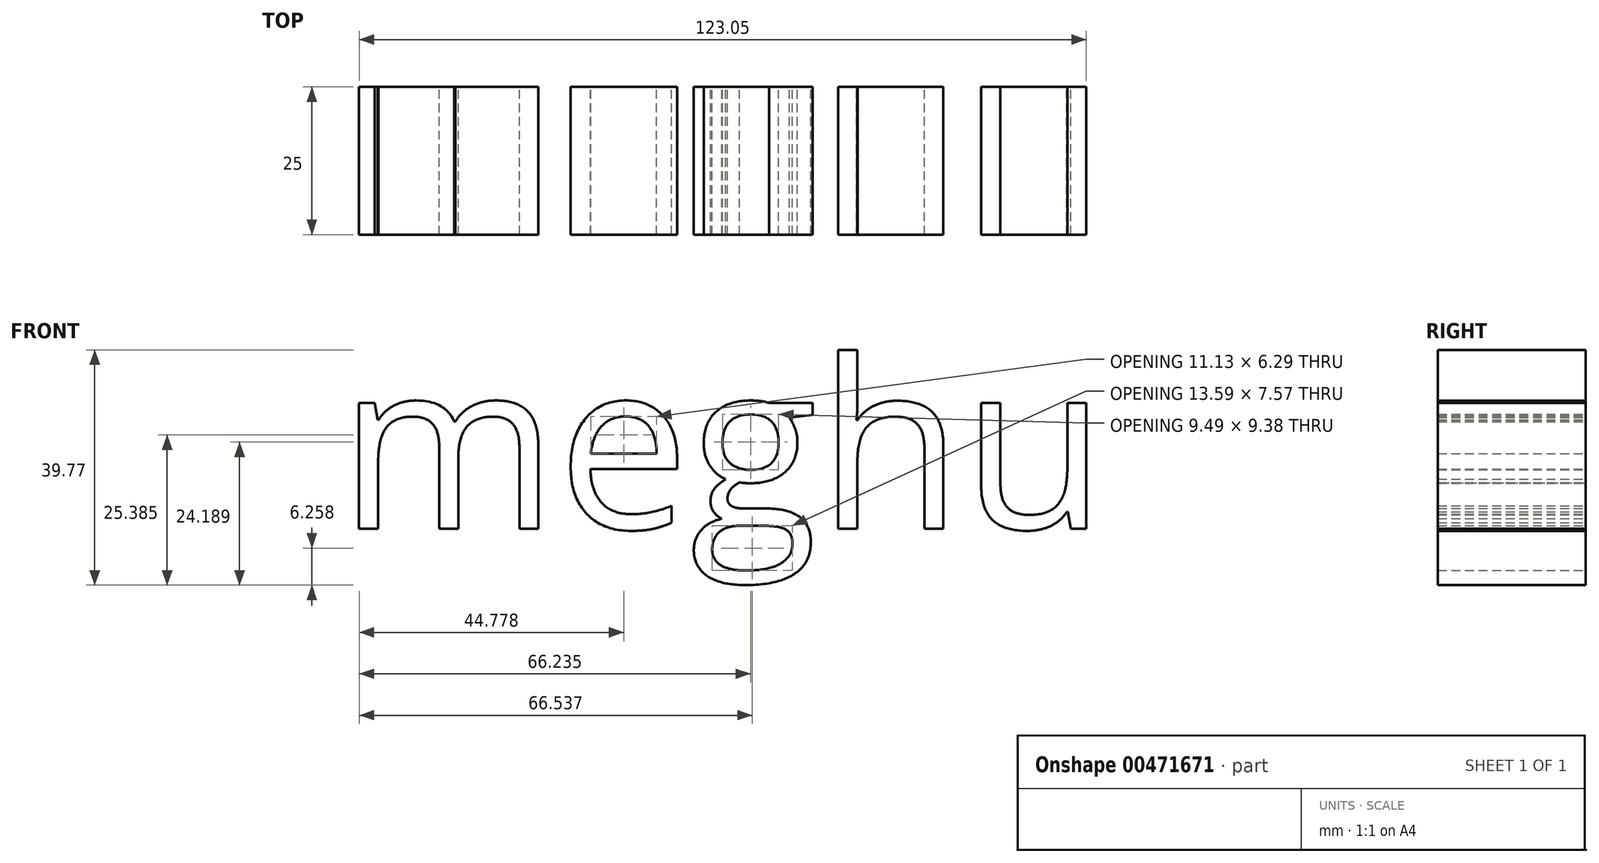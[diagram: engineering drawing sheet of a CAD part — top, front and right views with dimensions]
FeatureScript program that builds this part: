
annotation { "Feature Type Name" : "Feature", "Feature Type Description" : "" }
export const myFeature = defineFeature(function(context is Context, id is Id, definition is map)
    precondition{}
    {
        {
            var Q0;
            Q0=qCreatedBy(makeId("Front.planeOp"),FACE);
            var sketch = newSketch(context, id + "F0", { "sketchPlane" : qUnion([Q0])});
            skText(sketch, "E0", { "text": "meghu", "fontName": "OpenSans-Regular.ttf"});
            const initialGuessF0  = {"E0": [-0.04738, 0.0348, 1, 0, 0.02863]};
            skSetInitialGuess(sketch, initialGuessF0);
            skSolve(sketch);
        }
        {
            var Q0;
            Q0=makeQuery(id+"F0.imprint","IMPRINT",FACE,{"disambiguationData":[TD([[makeQuery(id+"F0.imprint","IMPRINT",EDGE,{"derivedFrom":sQuery(id+"F0.wireOp",EDGE,"E0.sketch_text.stroke-0")}),-1.0]])]});
            var Q1;
            Q1=makeQuery(id+"F0.imprint","IMPRINT",FACE,{"disambiguationData":[TD([[makeQuery(id+"F0.imprint","IMPRINT",EDGE,{"derivedFrom":sQuery(id+"F0.wireOp",EDGE,"E0.sketch_text.stroke-28")}),-1.0]])]});
            var Q2;
            Q2=makeQuery(id+"F0.imprint","IMPRINT",FACE,{"disambiguationData":[TD([[makeQuery(id+"F0.imprint","IMPRINT",EDGE,{"derivedFrom":sQuery(id+"F0.wireOp",EDGE,"E0.sketch_text.stroke-47")}),-1.0]])]});
            var Q3;
            Q3=makeQuery(id+"F0.imprint","IMPRINT",FACE,{"disambiguationData":[TD([[makeQuery(id+"F0.imprint","IMPRINT",EDGE,{"derivedFrom":sQuery(id+"F0.wireOp",EDGE,"E0.sketch_text.stroke-91")}),-1.0]])]});
            var Q4;
            Q4=makeQuery(id+"F0.imprint","IMPRINT",FACE,{"disambiguationData":[TD([[makeQuery(id+"F0.imprint","IMPRINT",EDGE,{"derivedFrom":sQuery(id+"F0.wireOp",EDGE,"E0.sketch_text.stroke-109")}),-1.0]])]});
            extrude(context, id + "F1", {"entities" : qUnion([Q0, Q1, Q2, Q3, Q4]), "depth" : 25 * mm});
        }
    });
